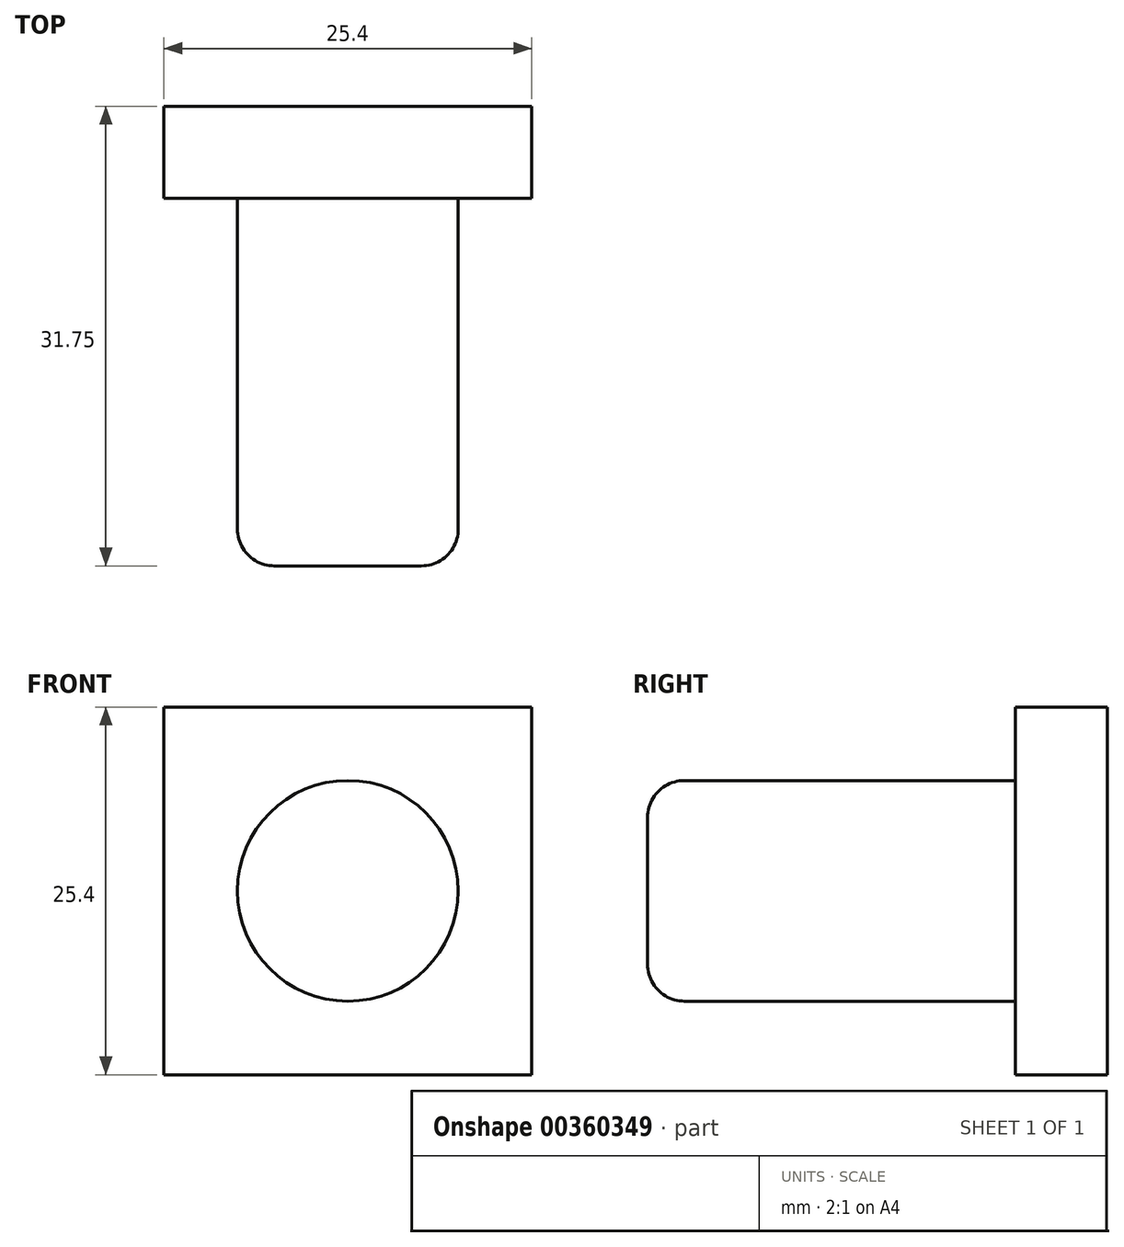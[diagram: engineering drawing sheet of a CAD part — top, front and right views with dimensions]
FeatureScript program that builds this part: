
annotation { "Feature Type Name" : "Feature", "Feature Type Description" : "" }
export const myFeature = defineFeature(function(context is Context, id is Id, definition is map)
    precondition{}
    {
        {
            var Q0;
            Q0=qCreatedBy(makeId("Front.planeOp"),FACE);
            var sketch = newSketch(context, id + "F0", { "sketchPlane" : qUnion([Q0])});
            skCircle(sketch, "E0", {"center": v(0, 6.58) * mm, "radius": 7.62 * mm});
            skSolve(sketch);
        }
        {
            var Q0;
            Q0 = qSketchRegion(id + "F0", true);
            extrude(context, id + "F1", {"entities" : qUnion([Q0]), "depth" : 25.4 * mm});
        }
        {
            var Q0;
            Q0=makeQuery(id+"F1.opExtrude","CAP_FACE",FACE,{"disambiguationData":[OSD([sQuery(id+"F0.wireOp",EDGE,"E0")])],"isStart":false});
            fillet(context, id + "F2", {"entities" : qUnion([Q0]), "radius" : 2.54 * mm, "tangentPropagation" : true, "allowEdgeOverflow" : false});
        }
        {
            var Q0;
            Q0=qCreatedBy(makeId("Front.planeOp"),FACE);
            var sketch = newSketch(context, id + "F3", { "sketchPlane" : qUnion([Q0])});
            skLineSegment(sketch, "E1", {"start": v(-12.7, 15.12) * mm, "end": v(-12.7, -6.12) * mm});
            skLineSegment(sketch, "E2", {"start": v(-12.7, -6.12) * mm, "end": v(12.7, -6.12) * mm});
            skLineSegment(sketch, "E3", {"start": v(12.7, -6.12) * mm, "end": v(12.7, 19.28) * mm});
            skLineSegment(sketch, "E4", {"start": v(12.7, 19.28) * mm, "end": v(-12.7, 19.28) * mm});
            skLineSegment(sketch, "E5", {"start": v(-12.7, 19.28) * mm, "end": v(-12.7, 15.12) * mm});
            skSolve(sketch);
        }
        {
            var Q0;
            Q0 = qSketchRegion(id + "F3", true);
            extrude(context, id + "F4", {"entities" : qUnion([Q0]), "operationType" : NewBodyOperationType.ADD, "oppositeDirection" : true, "depth" : 6.35 * mm});
        }
    });
